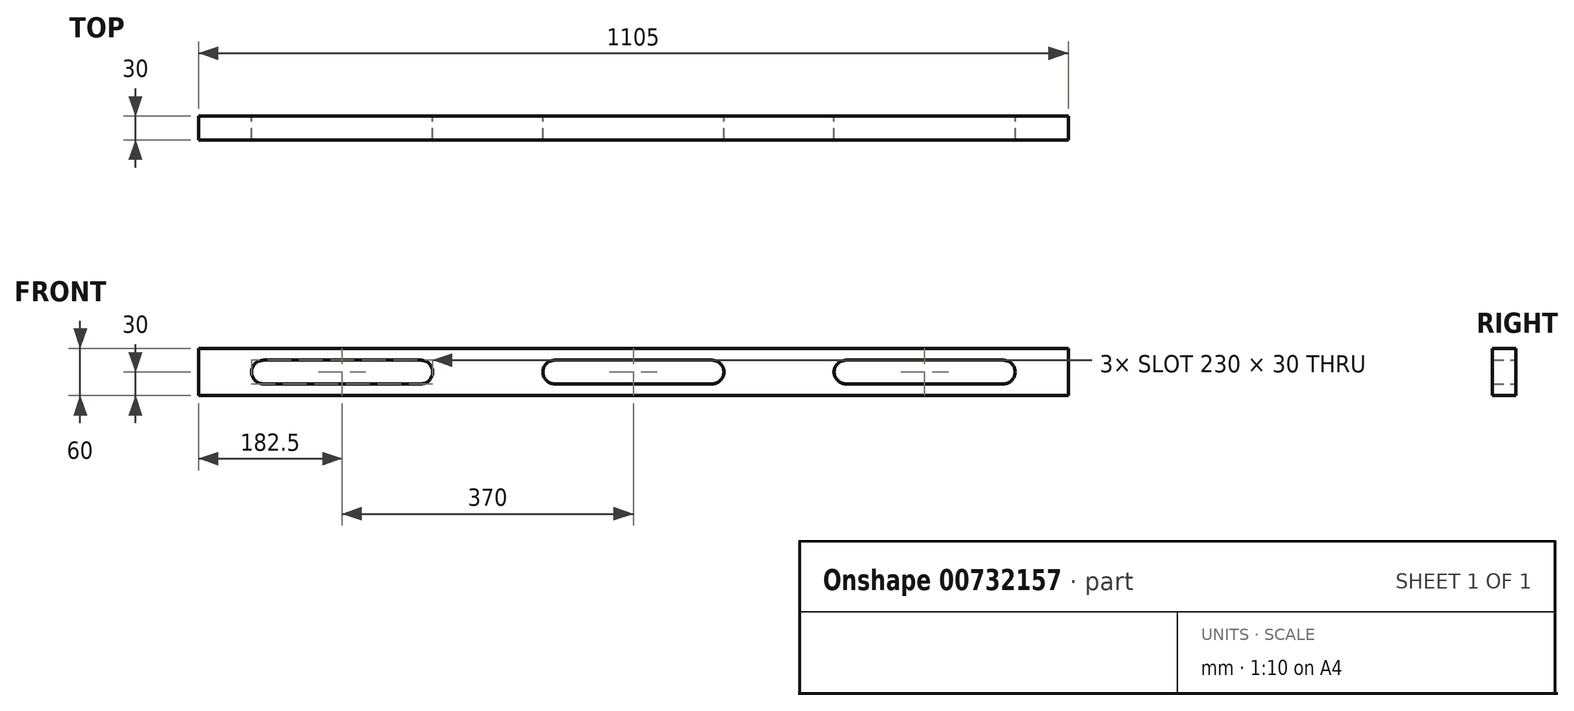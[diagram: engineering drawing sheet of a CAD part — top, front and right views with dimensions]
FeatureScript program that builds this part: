
annotation { "Feature Type Name" : "Feature", "Feature Type Description" : "" }
export const myFeature = defineFeature(function(context is Context, id is Id, definition is map)
    precondition{}
    {
        {
            var Q0;
            Q0=qCreatedBy(makeId("Front.planeOp"),FACE);
            var sketch = newSketch(context, id + "F0", { "sketchPlane" : qUnion([Q0])});
            skLineSegment(sketch, "E0.bottom", {"start": v(0, 0) * mm, "end": v(1175, 0) * mm});
            skLineSegment(sketch, "E0.top", {"start": v(0, 60) * mm, "end": v(1175, 60) * mm});
            skLineSegment(sketch, "E0.left", {"start": v(0, 0) * mm, "end": v(0, 60) * mm});
            skLineSegment(sketch, "E0.right", {"start": v(1175, 0) * mm, "end": v(1175, 60) * mm});
            skLineSegment(sketch, "E1.bottom", {"start": v(117.5, 15) * mm, "end": v(317.5, 15) * mm});
            skLineSegment(sketch, "E1.top", {"start": v(117.5, 45) * mm, "end": v(317.5, 45) * mm});
            skArc(sketch, "E2", {"start": v(117.5, 45) * mm, "mid": v(102.5, 30) * mm, "end": v(117.5, 15) * mm});
            skPoint(sketch, "E2.first.point", {"position": v(117.5, 15) * mm});
            skPoint(sketch, "E2.second.point", {"position": v(117.5, 45) * mm});
            skPoint(sketch, "E2.third.point", {"position": v(102.5, 30) * mm});
            skArc(sketch, "E3", {"start": v(317.5, 15) * mm, "mid": v(332.5, 30) * mm, "end": v(317.5, 45) * mm});
            skPoint(sketch, "E3.first.point", {"position": v(317.5, 15) * mm});
            skPoint(sketch, "E3.second.point", {"position": v(317.5, 45) * mm});
            skPoint(sketch, "E3.third.point", {"position": v(332.5, 30) * mm});
            skLineSegment(sketch, "E4.1.0.0", {"start": v(487.5, 15) * mm, "end": v(687.5, 15) * mm});
            skArc(sketch, "E4.1.0.2", {"start": v(687.5, 15) * mm, "mid": v(702.5, 30) * mm, "end": v(687.5, 45) * mm});
            skLineSegment(sketch, "E4.1.0.3", {"start": v(487.5, 45) * mm, "end": v(687.5, 45) * mm});
            skArc(sketch, "E4.1.0.4", {"start": v(487.5, 45) * mm, "mid": v(472.5, 30) * mm, "end": v(487.5, 15) * mm});
            skLineSegment(sketch, "E4.2.0.0", {"start": v(857.5, 15) * mm, "end": v(1057.5, 15) * mm});
            skArc(sketch, "E4.2.0.2", {"start": v(1057.5, 15) * mm, "mid": v(1072.5, 30) * mm, "end": v(1057.5, 45) * mm});
            skLineSegment(sketch, "E4.2.0.3", {"start": v(857.5, 45) * mm, "end": v(1057.5, 45) * mm});
            skArc(sketch, "E4.2.0.4", {"start": v(857.5, 45) * mm, "mid": v(842.5, 30) * mm, "end": v(857.5, 15) * mm});
            skLineSegment(sketch, "E4.direction1", {"start": v(117.5, 15) * mm, "end": v(487.5, 15) * mm, "construction": true});
            skSolve(sketch);
        }
        {
            var Q0;
            Q0=makeQuery(id+"F0.imprint","IMPRINT",FACE,{"disambiguationData":[TD([[makeQuery(id+"F0.imprint","IMPRINT",EDGE,{"derivedFrom":sQuery(id+"F0.wireOp",EDGE,"E0.bottom")}),1.0]])]});
            extrude(context, id + "F1", {"entities" : qUnion([Q0]), "depth" : 30 * mm, "offsetDistance" : 25 * mm});
        }
        {
            var Q0;
            Q0=makeQuery(id+"F1.opExtrude","CAP_FACE",FACE,{"disambiguationData":[OSD([sQuery(id+"F0.wireOp",EDGE,"E0.bottom"),sQuery(id+"F0.wireOp",EDGE,"E0.top"),sQuery(id+"F0.wireOp",EDGE,"E0.left"),sQuery(id+"F0.wireOp",EDGE,"E0.right"),sQuery(id+"F0.wireOp",EDGE,"E1.bottom"),sQuery(id+"F0.wireOp",EDGE,"E1.top"),sQuery(id+"F0.wireOp",EDGE,"E2"),sQuery(id+"F0.wireOp",EDGE,"E3"),sQuery(id+"F0.wireOp",EDGE,"E4.1.0.0"),sQuery(id+"F0.wireOp",EDGE,"E4.1.0.2"),sQuery(id+"F0.wireOp",EDGE,"E4.1.0.3"),sQuery(id+"F0.wireOp",EDGE,"E4.1.0.4"),sQuery(id+"F0.wireOp",EDGE,"E4.2.0.0"),sQuery(id+"F0.wireOp",EDGE,"E4.2.0.2"),sQuery(id+"F0.wireOp",EDGE,"E4.2.0.3"),sQuery(id+"F0.wireOp",EDGE,"E4.2.0.4"),sQuery(id+"F0.wireOp",EDGE,"E4.3.0.0"),sQuery(id+"F0.wireOp",EDGE,"E4.3.0.2"),sQuery(id+"F0.wireOp",EDGE,"E4.3.0.3"),sQuery(id+"F0.wireOp",EDGE,"E4.3.0.4"),sQuery(id+"F0.wireOp",EDGE,"E4.4.0.0"),sQuery(id+"F0.wireOp",EDGE,"E4.4.0.2"),sQuery(id+"F0.wireOp",EDGE,"E4.4.0.3"),sQuery(id+"F0.wireOp",EDGE,"E4.4.0.4")])],"isStart":false});
            var sketch = newSketch(context, id + "F2", { "sketchPlane" : qUnion([Q0])});
            skLineSegment(sketch, "E5.bottom", {"start": v(0, 0) * mm, "end": v(35, 0) * mm});
            skLineSegment(sketch, "E5.top", {"start": v(0, 60) * mm, "end": v(35, 60) * mm});
            skLineSegment(sketch, "E5.left", {"start": v(0, 0) * mm, "end": v(0, 60) * mm});
            skLineSegment(sketch, "E5.right", {"start": v(35, 0) * mm, "end": v(35, 60) * mm});
            skLineSegment(sketch, "E6.bottom", {"start": v(1140, 60) * mm, "end": v(1175, 60) * mm});
            skLineSegment(sketch, "E6.top", {"start": v(1140, 0) * mm, "end": v(1175, 0) * mm});
            skLineSegment(sketch, "E6.left", {"start": v(1140, 0) * mm, "end": v(1140, 60) * mm});
            skLineSegment(sketch, "E6.right", {"start": v(1175, 0) * mm, "end": v(1175, 60) * mm});
            skSolve(sketch);
        }
        {
            var Q0;
            Q0 = qSketchRegion(id + "F2", true);
            extrude(context, id + "F3", {"entities" : qUnion([Q0]), "operationType" : NewBodyOperationType.REMOVE, "oppositeDirection" : true, "depth" : 30 * mm, "offsetDistance" : 25 * mm});
        }
    });
